# Revit family: Accessory-Step_Can-KOHLER-K-23828_1
name_source: partatom
category: Specialty Equipment
units: mm (PartAtom-declared; Revit-internal decimal feet)

## family parameters
Cut with Voids When Loaded = No
Host = Face
OmniClass Number = 23.31.25.00
OmniClass Title = Toilet and Bath Specialties
Part Type = Normal
Room Calculation Point = No
Round Connector Dimension = Use Diameter
Shared = No

## types (3) — shared parameters
ADA Compliant = No
Assembly Code = C1030200
Date Modified = 02/23/2023
Default Elevation = 0"
Description = 82 Liter Dual Bin Step Can
Height = 26 7/16"
Length = 16 9/16"
Manufacturer = Kohler Co.
Master Format 2014 = 10 28 00
Master Format 2014 Name = Toilet, Bath, and Laundry Accessories
Material = Stainless Steel
Product Documentation Link = https://www.us.kohler.com
Product Page URL = http://www.us.kohler.com
URL = https://www.us.kohler.com
WaterSense Certified = No
Width = 22 15/16"

## per-type parameters (varying)
| type | Finish | Model | Secondary Finish | Type |
| ST-Stainless Steel | KOHLER-Metal-ST-Stainless_Steel | K-23828-ST | Kohler-Plastic-7-Black_Black | 2 |
| BST-Black Stainless | KOHLER-Metal-BST-Black_Stainless | K-23828-BST | Kohler-Plastic-7-Black_Black | 1 |
| STW-White and Stainless Steel | KOHLER-Metal-STW-White_and_Stainless_Steel | K-23828-STW | Kohler-Plastic-0-White | 3 |

## geometry (parser evidence)
native form markers: Sweep x5
no freeform markers — native parametric forms only
